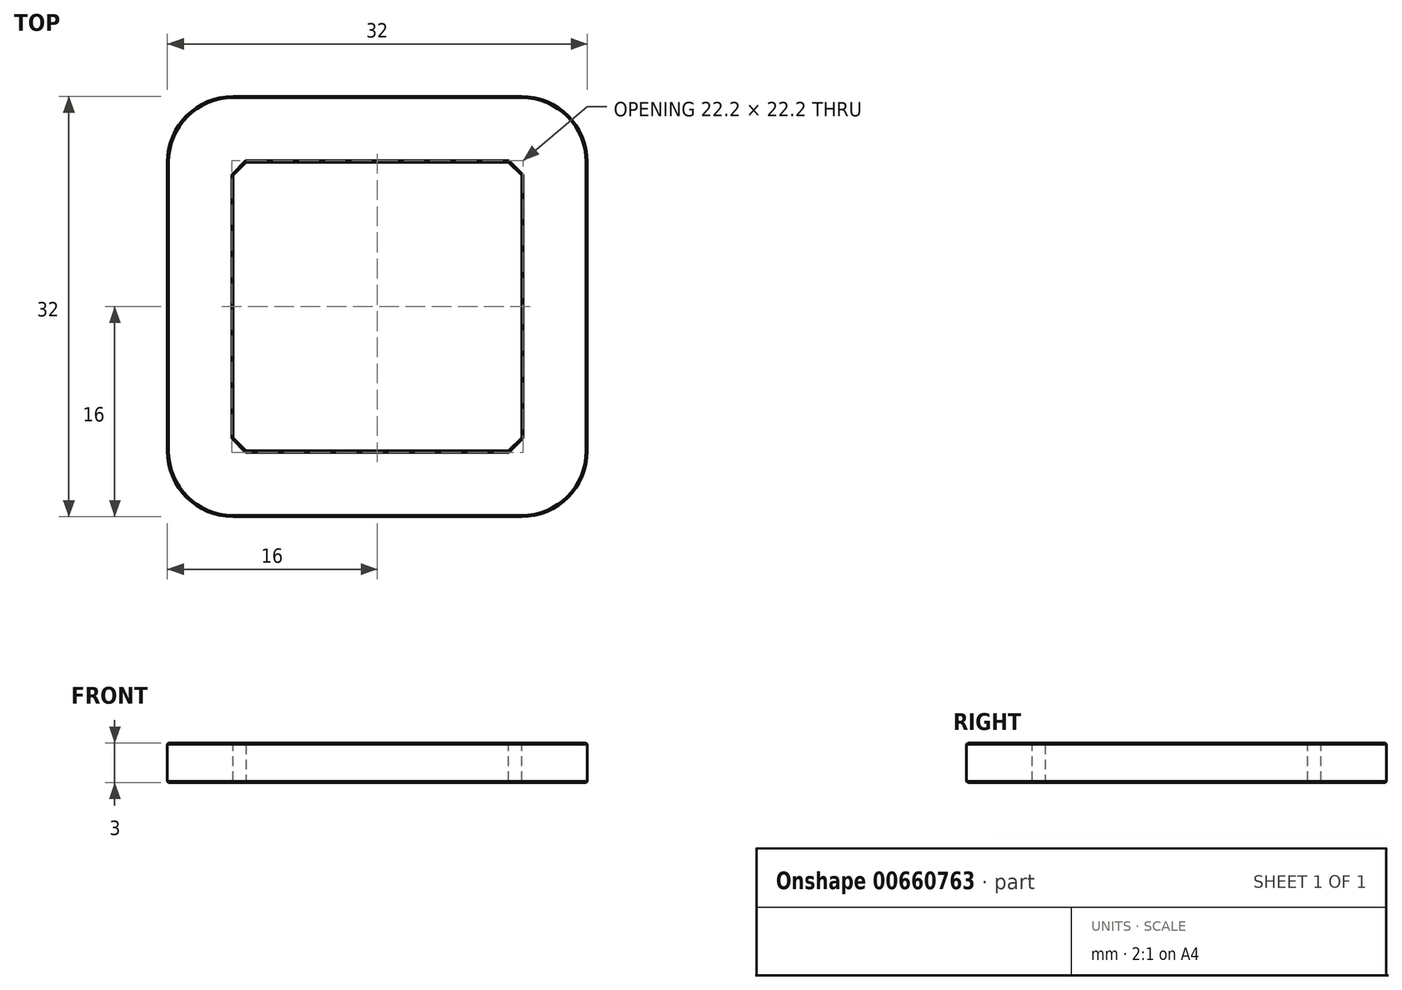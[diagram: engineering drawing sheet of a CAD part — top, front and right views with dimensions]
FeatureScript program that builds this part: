
annotation { "Feature Type Name" : "Feature", "Feature Type Description" : "" }
export const myFeature = defineFeature(function(context is Context, id is Id, definition is map)
    precondition{}
    {
        {
            var Q0;
            Q0=qCreatedBy(makeId("Top.planeOp"),FACE);
            var sketch = newSketch(context, id + "F0", { "sketchPlane" : qUnion([Q0])});
            skLineSegment(sketch, "E0.bottom", {"start": v(-16, 16) * mm, "end": v(16, 16) * mm});
            skLineSegment(sketch, "E0.top", {"start": v(-16, -16) * mm, "end": v(16, -16) * mm});
            skLineSegment(sketch, "E0.left", {"start": v(-16, 16) * mm, "end": v(-16, -16) * mm});
            skLineSegment(sketch, "E0.right", {"start": v(16, 16) * mm, "end": v(16, -16) * mm});
            skPoint(sketch, "E0.middle", {"position": v(0, 0) * mm});
            skLineSegment(sketch, "E1.bottom", {"start": v(-11, 11) * mm, "end": v(11, 11) * mm});
            skLineSegment(sketch, "E1.top", {"start": v(-11, -11) * mm, "end": v(11, -11) * mm});
            skLineSegment(sketch, "E1.left", {"start": v(-11, 11) * mm, "end": v(-11, -11) * mm});
            skLineSegment(sketch, "E1.right", {"start": v(11, 11) * mm, "end": v(11, -11) * mm});
            skSolve(sketch);
        }
        {
            var Q0;
            Q0=makeQuery(id+"F0.imprint","IMPRINT",FACE,{"disambiguationData":[TD([[makeQuery(id+"F0.imprint","IMPRINT",EDGE,{"derivedFrom":sQuery(id+"F0.wireOp",EDGE,"E0.bottom")}),-1.0]])]});
            extrude(context, id + "F1", {"entities" : qUnion([Q0]), "depth" : 3 * mm, "offsetDistance" : 25 * mm});
        }
        {
            var Q0;
            Q0=makeQuery(id+"F1.opExtrude","SWEPT_EDGE",EDGE,{"disambiguationData":[OSD([sQuery(id+"F0.wireOp",EDGE,"E1.bottom"),sQuery(id+"F0.wireOp",EDGE,"E1.left")])]});
            var Q1;
            Q1=makeQuery(id+"F1.opExtrude","SWEPT_EDGE",EDGE,{"disambiguationData":[OSD([sQuery(id+"F0.wireOp",EDGE,"E1.top"),sQuery(id+"F0.wireOp",EDGE,"E1.left")])]});
            var Q2;
            Q2=makeQuery(id+"F1.opExtrude","SWEPT_EDGE",EDGE,{"disambiguationData":[OSD([sQuery(id+"F0.wireOp",EDGE,"E1.bottom"),sQuery(id+"F0.wireOp",EDGE,"E1.right")])]});
            var Q3;
            Q3=makeQuery(id+"F1.opExtrude","SWEPT_EDGE",EDGE,{"disambiguationData":[OSD([sQuery(id+"F0.wireOp",EDGE,"E1.top"),sQuery(id+"F0.wireOp",EDGE,"E1.right")])]});
            chamfer(context, id + "F2", {"entities" : qUnion([Q0, Q1, Q2, Q3]), "chamferType" : ChamferType.TWO_OFFSETS, "width1" : 1 * mm, "oppositeDirection" : false, "width2" : 1 * mm, "tangentPropagation" : true});
        }
        {
            var Q0;
            Q0=makeQuery(id+"F1.opExtrude","SWEPT_EDGE",EDGE,{"disambiguationData":[OSD([sQuery(id+"F0.wireOp",EDGE,"E0.bottom"),sQuery(id+"F0.wireOp",EDGE,"E0.right")])]});
            var Q1;
            Q1=makeQuery(id+"F1.opExtrude","SWEPT_EDGE",EDGE,{"disambiguationData":[OSD([sQuery(id+"F0.wireOp",EDGE,"E0.top"),sQuery(id+"F0.wireOp",EDGE,"E0.right")])]});
            var Q2;
            Q2=makeQuery(id+"F1.opExtrude","SWEPT_EDGE",EDGE,{"disambiguationData":[OSD([sQuery(id+"F0.wireOp",EDGE,"E0.top"),sQuery(id+"F0.wireOp",EDGE,"E0.left")])]});
            var Q3;
            Q3=makeQuery(id+"F1.opExtrude","SWEPT_EDGE",EDGE,{"disambiguationData":[OSD([sQuery(id+"F0.wireOp",EDGE,"E0.bottom"),sQuery(id+"F0.wireOp",EDGE,"E0.left")])]});
            fillet(context, id + "F3", {"entities" : qUnion([Q0, Q1, Q2, Q3]), "radius" : 5 * mm, "tangentPropagation" : true, "allowEdgeOverflow" : false});
        }
        {
            var Q0;
            Q0=makeQuery(id+"F1.opExtrude","CAP_FACE",FACE,{"disambiguationData":[OSD([sQuery(id+"F0.wireOp",EDGE,"E0.bottom"),sQuery(id+"F0.wireOp",EDGE,"E0.top"),sQuery(id+"F0.wireOp",EDGE,"E0.left"),sQuery(id+"F0.wireOp",EDGE,"E0.right"),sQuery(id+"F0.wireOp",EDGE,"E1.bottom"),sQuery(id+"F0.wireOp",EDGE,"E1.top"),sQuery(id+"F0.wireOp",EDGE,"E1.left"),sQuery(id+"F0.wireOp",EDGE,"E1.right")])],"isStart":false});
            var Q1;
            Q1=makeQuery(id+"F1.opExtrude","CAP_FACE",FACE,{"disambiguationData":[OSD([sQuery(id+"F0.wireOp",EDGE,"E0.bottom"),sQuery(id+"F0.wireOp",EDGE,"E0.top"),sQuery(id+"F0.wireOp",EDGE,"E0.left"),sQuery(id+"F0.wireOp",EDGE,"E0.right"),sQuery(id+"F0.wireOp",EDGE,"E1.bottom"),sQuery(id+"F0.wireOp",EDGE,"E1.top"),sQuery(id+"F0.wireOp",EDGE,"E1.left"),sQuery(id+"F0.wireOp",EDGE,"E1.right")])],"isStart":true});
            chamfer(context, id + "F4", {"entities" : qUnion([Q0, Q1]), "width" : 0.1 * mm, "tangentPropagation" : true});
        }
    });
